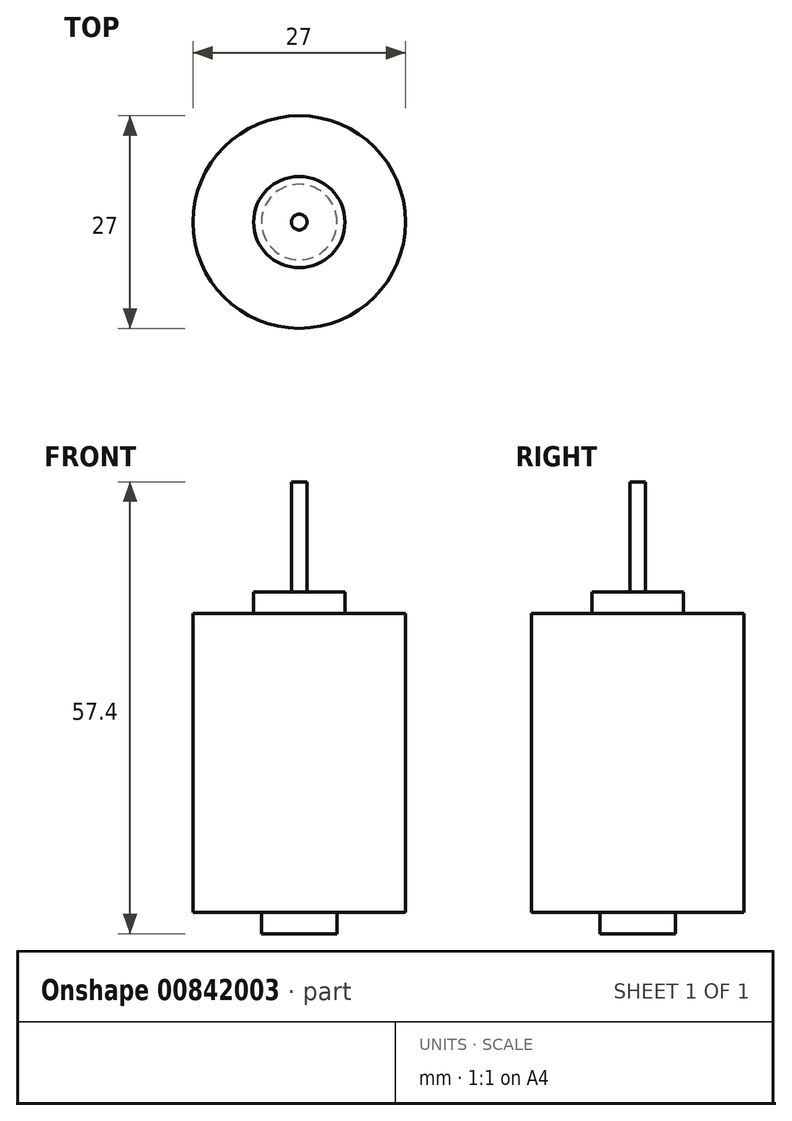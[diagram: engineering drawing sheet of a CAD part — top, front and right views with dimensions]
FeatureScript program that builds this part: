
annotation { "Feature Type Name" : "Feature", "Feature Type Description" : "" }
export const myFeature = defineFeature(function(context is Context, id is Id, definition is map)
    precondition{}
    {
        {
            var Q0;
            Q0=qCreatedBy(makeId("Right.planeOp"),FACE);
            var sketch = newSketch(context, id + "F0", { "sketchPlane" : qUnion([Q0])});
            skLineSegment(sketch, "E0", {"start": v(-63.46, 10.8) * mm, "end": v(-63.46, -46.6) * mm});
            skLineSegment(sketch, "E1", {"start": v(-63.46, -46.6) * mm, "end": v(-58.66, -46.6) * mm});
            skLineSegment(sketch, "E2", {"start": v(-58.66, -46.6) * mm, "end": v(-58.66, -43.9) * mm});
            skLineSegment(sketch, "E3", {"start": v(-58.66, -43.9) * mm, "end": v(-49.96, -43.9) * mm});
            skLineSegment(sketch, "E4", {"start": v(-49.96, -43.9) * mm, "end": v(-49.96, -5.9) * mm});
            skLineSegment(sketch, "E5", {"start": v(-49.96, -5.9) * mm, "end": v(-57.66, -5.9) * mm});
            skLineSegment(sketch, "E6", {"start": v(-57.66, -5.9) * mm, "end": v(-57.66, -3.2) * mm});
            skLineSegment(sketch, "E7", {"start": v(-57.66, -3.2) * mm, "end": v(-62.46, -3.2) * mm});
            skLineSegment(sketch, "E8", {"start": v(-62.46, -3.2) * mm, "end": v(-62.46, 10.8) * mm});
            skLineSegment(sketch, "E9", {"start": v(-62.46, 10.8) * mm, "end": v(-63.46, 10.8) * mm});
            skSolve(sketch);
        }
        {
            var Q0;
            Q0=makeQuery(id+"F0.imprint","IMPRINT",FACE,{"disambiguationData":[TD([[makeQuery(id+"F0.imprint","IMPRINT",EDGE,{"derivedFrom":sQuery(id+"F0.wireOp",EDGE,"E0")}),1.0]])]});
            var Q1;
            Q1=sQuery(id+"F0.wireOp",EDGE,"E0");
            revolve(context, id + "F1", {"surfaceOperationType" : NewSurfaceOperationType.NEW, "entities" : qUnion([Q0]), "axis" : qUnion([Q1]), "revolveType" : RevolveType.FULL});
        }
        {
            var Q0;
            Q0=qCreatedBy(makeId("Front.planeOp"),FACE);
            cPlane(context, id + "F2", {"entities" : qUnion([Q0]), "cplaneType" : CPlaneType.OFFSET, "offset" : 30.8 * mm, "width" : 150 * mm, "height" : 150 * mm});
        }
        {
            var Q0;
            Q0=qCreatedBy(id+"F2.planeOp",FACE);
            cPlane(context, id + "F3", {"entities" : qUnion([Q0]), "cplaneType" : CPlaneType.OFFSET, "offset" : 25 * mm, "width" : 150 * mm, "height" : 150 * mm});
        }
    });
